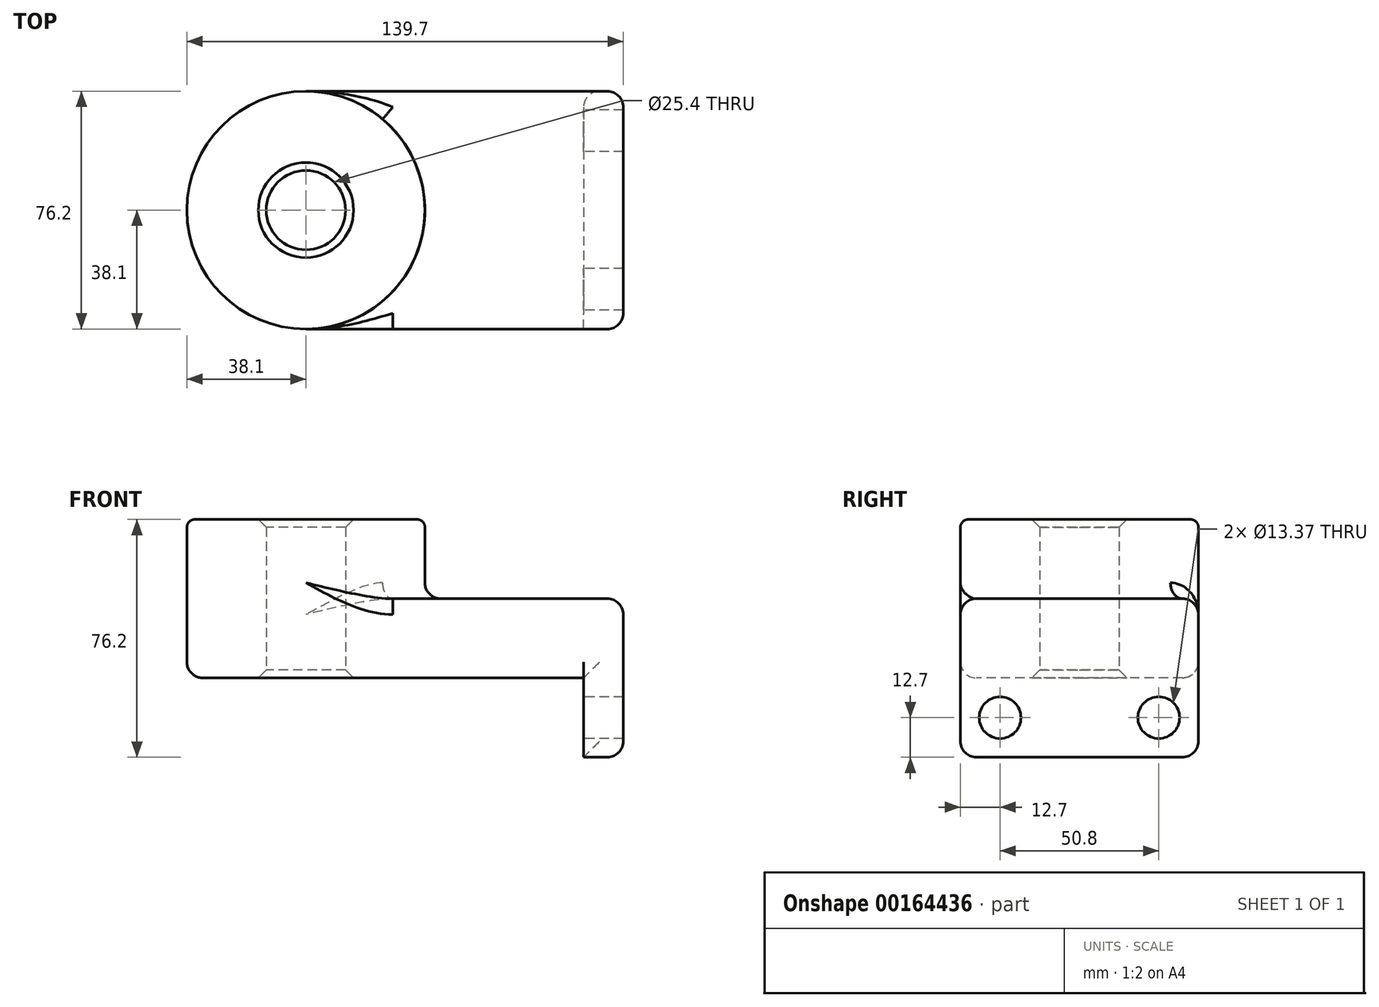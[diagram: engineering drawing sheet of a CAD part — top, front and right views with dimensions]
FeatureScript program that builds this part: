
annotation { "Feature Type Name" : "Feature", "Feature Type Description" : "" }
export const myFeature = defineFeature(function(context is Context, id is Id, definition is map)
    precondition{}
    {
        {
            var Q0;
            Q0=qCreatedBy(makeId("Top.planeOp"),FACE);
            var sketch = newSketch(context, id + "F0", { "sketchPlane" : qUnion([Q0])});
            skLineSegment(sketch, "E0.bottom", {"start": v(-44.45, 38.1) * mm, "end": v(44.45, 38.1) * mm});
            skLineSegment(sketch, "E0.top", {"start": v(-44.45, -38.1) * mm, "end": v(44.45, -38.1) * mm});
            skLineSegment(sketch, "E0.left", {"start": v(-44.45, 38.1) * mm, "end": v(-44.45, -38.1) * mm});
            skLineSegment(sketch, "E0.right", {"start": v(44.45, 38.1) * mm, "end": v(44.45, -38.1) * mm});
            skPoint(sketch, "E0.middle", {"position": v(0, 0) * mm});
            skCircle(sketch, "E1", {"center": v(-44.45, 0) * mm, "radius": 38.1 * mm});
            skCircle(sketch, "E2", {"center": v(-44.45, 0) * mm, "radius": 12.7 * mm});
            skSolve(sketch);
        }
        {
            var Q0;
            {var subQ0=sQuery(id+"F0.wireOp",EDGE,"E0.left");Q0=makeQuery(id+"F0.imprint","IMPRINT",FACE,{"disambiguationData":[TD([[makeQuery(id+"F0.imprint","IMPRINT",EDGE,{"derivedFrom":subQ0}),-1.0]])]});}
            var Q1;
            {var subQ0=sQuery(id+"F0.wireOp",EDGE,"E0.left");Q1=makeQuery(id+"F0.imprint","IMPRINT",FACE,{"disambiguationData":[TD([[makeQuery(id+"F0.imprint","IMPRINT",EDGE,{"derivedFrom":subQ0}),1.0]])]});}
            var Q2;
            {var subQ0=sQuery(id+"F0.wireOp",EDGE,"E0.bottom");Q2=makeQuery(id+"F0.imprint","IMPRINT",FACE,{"disambiguationData":[TD([[makeQuery(id+"F0.imprint","IMPRINT",EDGE,{"derivedFrom":subQ0}),-1.0]])]});}
            extrude(context, id + "F1", {"entities" : qUnion([Q0, Q1, Q2]), "depth" : 25.4 * mm});
        }
        {
            var Q0;
            {var subQ1=sQuery(id+"F0.wireOp",EDGE,"E0.left");var subQ3=sQuery(id+"F0.wireOp",EDGE,"E2");var subQ4=makeQuery(id+"F0.imprint","INTERSECT",VERTEX,{"disambiguationData":[OD(0.0)],"derivedFrom":[subQ1,subQ3]});Q0=makeQuery(id+"F0.imprint","IMPRINT",FACE,{"disambiguationData":[TD([[makeQuery(id+"F0.imprint","IMPRINT",EDGE,{"disambiguationData":[TD([[subQ4,1.0]])],"derivedFrom":subQ3}),-1.0]])]});}
            var Q1;
            {var subQ1=sQuery(id+"F0.wireOp",EDGE,"E0.left");var subQ3=sQuery(id+"F0.wireOp",EDGE,"E2");var subQ4=makeQuery(id+"F0.imprint","INTERSECT",VERTEX,{"disambiguationData":[OD(0.0)],"derivedFrom":[subQ1,subQ3]});Q1=makeQuery(id+"F0.imprint","IMPRINT",FACE,{"disambiguationData":[TD([[makeQuery(id+"F0.imprint","IMPRINT",EDGE,{"disambiguationData":[TD([[subQ4,-1.0]])],"derivedFrom":subQ3}),-1.0]])]});}
            extrude(context, id + "F2", {"entities" : qUnion([Q0, Q1]), "operationType" : NewBodyOperationType.ADD, "depth" : 50.8 * mm});
        }
        {
            var Q0;
            Q0=makeQuery(id+"F1.opExtrude","SWEPT_FACE",FACE,{"disambiguationData":[OSD([sQuery(id+"F0.wireOp",EDGE,"E0.right")])]});
            var sketch = newSketch(context, id + "F3", { "sketchPlane" : qUnion([Q0])});
            skLineSegment(sketch, "E3.bottom", {"start": v(-38.1, 25.4) * mm, "end": v(38.1, 25.4) * mm, "construction": true});
            skLineSegment(sketch, "E3.top", {"start": v(-38.1, -25.4) * mm, "end": v(38.1, -25.4) * mm});
            skLineSegment(sketch, "E3.left", {"start": v(-38.1, 25.4) * mm, "end": v(-38.1, -25.4) * mm});
            skLineSegment(sketch, "E3.right", {"start": v(38.1, 25.4) * mm, "end": v(38.1, -25.4) * mm});
            skLineSegment(sketch, "E4", {"start": v(0, 0) * mm, "end": v(0, -25.4) * mm, "construction": true});
            skCircle(sketch, "E5", {"center": v(25.4, -12.7) * mm, "radius": 6.68 * mm});
            skCircle(sketch, "E6.MirrorC", {"center": v(-25.4, -12.7) * mm, "radius": 6.68 * mm});
            skSolve(sketch);
        }
        {
            var Q0;
            {var subQ0=sQuery(id+"F3.wireOp",EDGE,"E3.top");Q0=makeQuery(id+"F3.imprint","IMPRINT",FACE,{"disambiguationData":[TD([[makeQuery(id+"F3.imprint","IMPRINT",EDGE,{"derivedFrom":subQ0}),1.0]])]});}
            var Q1;
            {var subQ1=sQuery(id+"F0.wireOp",EDGE,"E0.right");var subQ2=makeQuery(id+"F1.opExtrude","CAP_EDGE",EDGE,{"disambiguationData":[OSD([subQ1])],"isStart":true});Q1=makeQuery(id+"F3.imprint","IMPRINT",FACE,{"disambiguationData":[TD([[makeQuery(id+"F3.imprint","IMPRINT",EDGE,{"derivedFrom":subQ2}),-1.0]])]});}
            extrude(context, id + "F4", {"entities" : qUnion([Q0, Q1]), "operationType" : NewBodyOperationType.ADD, "depth" : 12.7 * mm});
        }
        {
            var Q0;
            {var subQ0=sQuery(id+"F0.wireOp",EDGE,"E1");Q0=makeQuery(id+"F2.boolean.opBoolean","INTERSECT",EDGE,{"derivedFrom":[makeQuery(id+"F1.opExtrude","CAP_FACE",FACE,{"disambiguationData":[OSD([sQuery(id+"F0.wireOp",EDGE,"E0.bottom"),sQuery(id+"F0.wireOp",EDGE,"E0.top"),sQuery(id+"F0.wireOp",EDGE,"E0.right"),subQ0,sQuery(id+"F0.wireOp",EDGE,"E2")])],"isStart":false}),makeQuery(id+"F2.opExtrude","SWEPT_FACE",FACE,{"disambiguationData":[OSD([subQ0])]})]});}
            var Q1;
            Q1=makeQuery(id+"F4.boolean.opBoolean","MERGE",EDGE,{"derivedFrom":[makeQuery(id+"F1.opExtrude","CAP_EDGE",EDGE,{"disambiguationData":[OSD([sQuery(id+"F0.wireOp",EDGE,"E0.bottom")])],"isStart":false}),makeQuery(id+"F4.opExtrude","SWEPT_EDGE",EDGE,{"disambiguationData":[OSD([sQuery(id+"F0.wireOp",EDGE,"E0.right"),sQuery(id+"F3.wireOp",EDGE,"E3.right")])]})]});
            var Q2;
            Q2=makeQuery(id+"F1.opExtrude","CAP_EDGE",EDGE,{"disambiguationData":[OSD([sQuery(id+"F0.wireOp",EDGE,"E0.bottom")])],"isStart":true});
            var Q3;
            Q3=makeQuery(id+"F4.opExtrude","CAP_EDGE",EDGE,{"disambiguationData":[OSD([sQuery(id+"F3.wireOp",EDGE,"E3.right")])],"isStart":true});
            var Q4;
            Q4=makeQuery(id+"F4.opExtrude","CAP_EDGE",EDGE,{"disambiguationData":[OSD([sQuery(id+"F3.wireOp",EDGE,"E3.left")])],"isStart":false});
            var Q5;
            Q5=makeQuery(id+"F4.opExtrude","CAP_EDGE",EDGE,{"disambiguationData":[OSD([sQuery(id+"F3.wireOp",EDGE,"E3.top")])],"isStart":false});
            var Q6;
            Q6=makeQuery(id+"F4.opExtrude","SWEPT_EDGE",EDGE,{"disambiguationData":[OSD([sQuery(id+"F3.wireOp",EDGE,"E3.top"),sQuery(id+"F3.wireOp",EDGE,"E3.right")])]});
            var Q7;
            Q7=makeQuery(id+"F4.opExtrude","SWEPT_EDGE",EDGE,{"disambiguationData":[OSD([sQuery(id+"F3.wireOp",EDGE,"E3.top"),sQuery(id+"F3.wireOp",EDGE,"E3.left")])]});
            fillet(context, id + "F5", {"entities" : qUnion([Q0, Q1, Q2, Q3, Q4, Q5, Q6, Q7]), "radius" : 5.08 * mm, "tangentPropagation" : true, "allowEdgeOverflow" : false});
        }
        {
            var Q0;
            Q0=makeQuery(id+"F2.opExtrude","CAP_EDGE",EDGE,{"disambiguationData":[OSD([sQuery(id+"F0.wireOp",EDGE,"E2")])],"isStart":false});
            chamfer(context, id + "F6", {"entities" : qUnion([Q0]), "width" : 2.54 * mm, "tangentPropagation" : true});
        }
        {
            var Q0;
            Q0=makeQuery(id+"F1.opExtrude","CAP_EDGE",EDGE,{"disambiguationData":[OSD([sQuery(id+"F0.wireOp",EDGE,"E2")])],"isStart":true});
            chamfer(context, id + "F7", {"entities" : qUnion([Q0]), "width" : 2.54 * mm, "tangentPropagation" : true});
        }
        {
            var Q0;
            Q0=makeQuery(id+"F4.opExtrude","CAP_EDGE",EDGE,{"disambiguationData":[OSD([sQuery(id+"F0.wireOp",EDGE,"E0.right")])],"isStart":false});
            fillet(context, id + "F8", {"entities" : qUnion([Q0]), "radius" : 5.08 * mm, "tangentPropagation" : true, "allowEdgeOverflow" : false});
        }
        {
            var Q0;
            Q0=makeQuery(id+"F2.opExtrude","CAP_EDGE",EDGE,{"disambiguationData":[OSD([sQuery(id+"F0.wireOp",EDGE,"E1")])],"isStart":false});
            fillet(context, id + "F9", {"entities" : qUnion([Q0]), "radius" : 2.54 * mm, "tangentPropagation" : true, "allowEdgeOverflow" : false});
        }
    });
